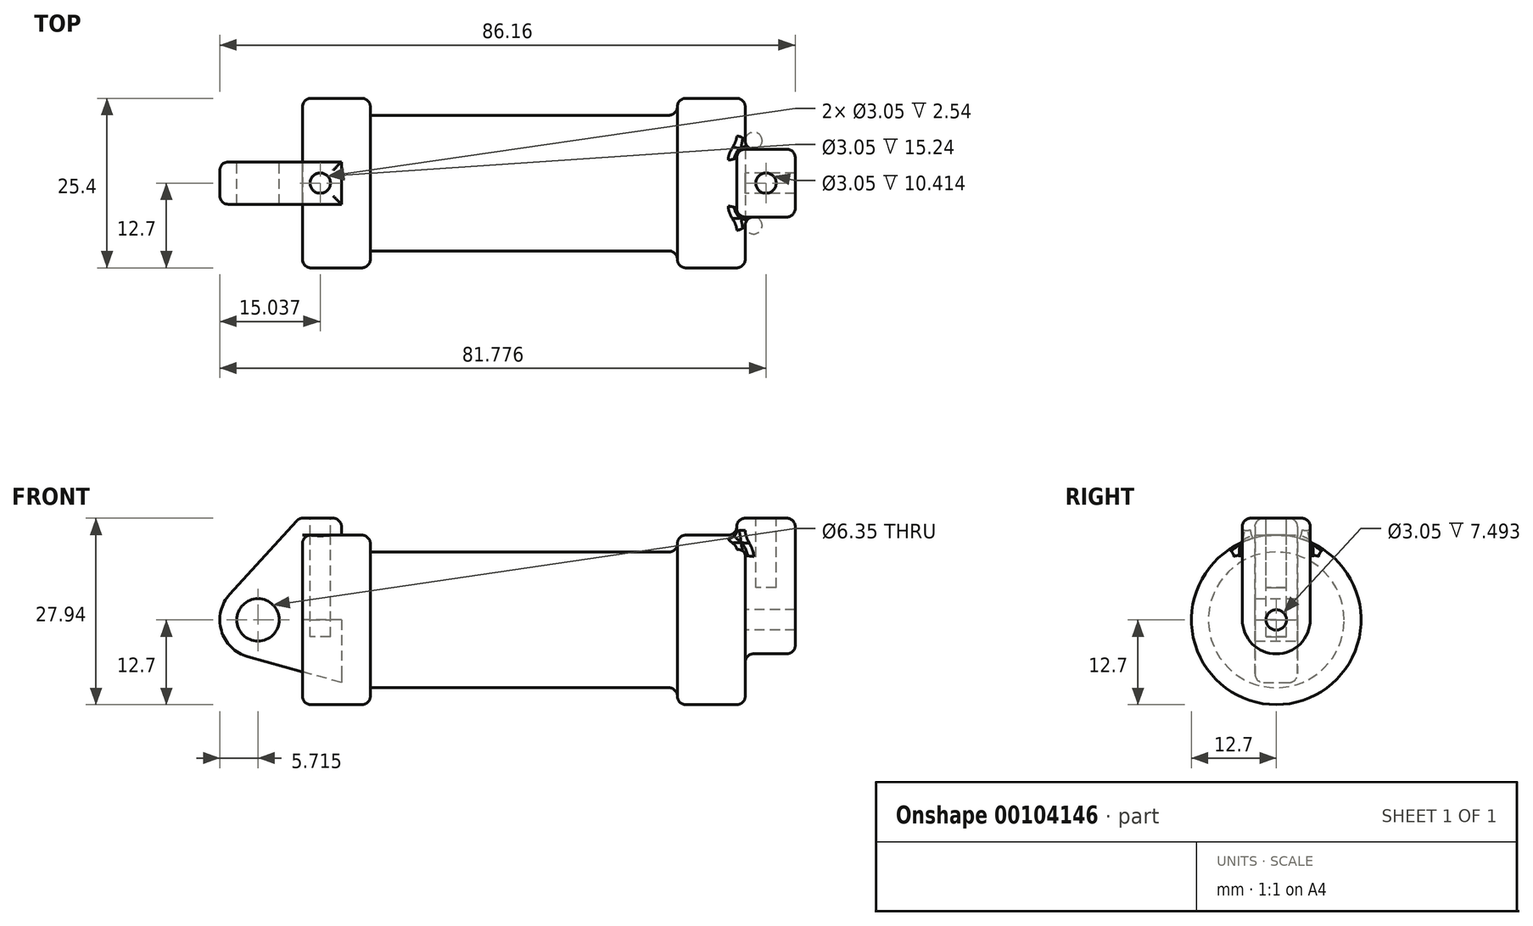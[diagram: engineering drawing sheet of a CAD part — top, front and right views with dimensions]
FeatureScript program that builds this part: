
annotation { "Feature Type Name" : "Feature", "Feature Type Description" : "" }
export const myFeature = defineFeature(function(context is Context, id is Id, definition is map)
    precondition{}
    {
        {
            var Q0;
            Q0=qCreatedBy(makeId("Front.planeOp"),FACE);
            var sketch = newSketch(context, id + "F0", { "sketchPlane" : qUnion([Q0])});
            skLineSegment(sketch, "E0", {"start": v(0, 0) * mm, "end": v(0, 12.7) * mm});
            skLineSegment(sketch, "E1", {"start": v(0, 12.7) * mm, "end": v(10.16, 12.7) * mm});
            skLineSegment(sketch, "E2", {"start": v(10.16, 12.7) * mm, "end": v(10.16, 10.16) * mm});
            skLineSegment(sketch, "E3", {"start": v(10.16, 10.16) * mm, "end": v(56.13, 10.16) * mm});
            skLineSegment(sketch, "E4", {"start": v(56.13, 10.16) * mm, "end": v(56.13, 12.7) * mm});
            skLineSegment(sketch, "E5", {"start": v(56.13, 12.7) * mm, "end": v(66.3, 12.7) * mm});
            skLineSegment(sketch, "E6", {"start": v(66.3, 12.7) * mm, "end": v(66.3, 0) * mm});
            skLineSegment(sketch, "E7", {"start": v(66.3, 0) * mm, "end": v(0, 0) * mm});
            skLineSegment(sketch, "E8", {"start": v(5.84, 15.24) * mm, "end": v(-0.5, 15.24) * mm});
            skLineSegment(sketch, "E9", {"start": v(-0.5, 15.24) * mm, "end": v(-10.88, 3.85) * mm});
            skLineSegment(sketch, "E10", {"start": v(0, 0) * mm, "end": v(-6.65, 0) * mm});
            skCircle(sketch, "E11", {"center": v(-6.65, 0) * mm, "radius": 5.72 * mm});
            skCircle(sketch, "E12", {"center": v(-6.65, 0) * mm, "radius": 3.18 * mm});
            skLineSegment(sketch, "E13", {"start": v(5.84, 15.24) * mm, "end": v(5.84, -9.4) * mm});
            skLineSegment(sketch, "E14", {"start": v(5.84, -9.4) * mm, "end": v(-8.18, -5.5) * mm});
            skSolve(sketch);
        }
        {
            var Q0;
            {var subQ0=sQuery(id+"F0.wireOp",EDGE,"E2");Q0=makeQuery(id+"F0.imprint","IMPRINT",FACE,{"disambiguationData":[TD([[makeQuery(id+"F0.imprint","IMPRINT",EDGE,{"derivedFrom":subQ0}),-1.0]])]});}
            var Q1;
            Q1=sQuery(id+"F0.wireOp",EDGE,"E7");
            revolve(context, id + "F1", {"entities" : qUnion([Q0]), "axis" : qUnion([Q1]), "revolveType" : RevolveType.FULL});
        }
        {
            var Q0;
            {var subQ0=sQuery(id+"F0.wireOp",EDGE,"E0");Q0=makeQuery(id+"F0.imprint","IMPRINT",FACE,{"disambiguationData":[TD([[makeQuery(id+"F0.imprint","IMPRINT",EDGE,{"derivedFrom":subQ0}),-1.0]])]});}
            var Q1;
            Q1=sQuery(id+"F0.wireOp",EDGE,"E7");
            revolve(context, id + "F2", {"operationType" : NewBodyOperationType.ADD, "entities" : qUnion([Q0]), "axis" : qUnion([Q1]), "revolveType" : RevolveType.FULL});
        }
        {
            var Q0;
            {var subQ3=sQuery(id+"F0.wireOp",EDGE,"E0");Q0=makeQuery(id+"F0.imprint","IMPRINT",FACE,{"disambiguationData":[TD([[makeQuery(id+"F0.imprint","IMPRINT",EDGE,{"derivedFrom":subQ3}),1.0]])]});}
            var Q1;
            {var subQ0=sQuery(id+"F0.wireOp",EDGE,"E14");Q1=makeQuery(id+"F0.imprint","IMPRINT",FACE,{"disambiguationData":[TD([[makeQuery(id+"F0.imprint","IMPRINT",EDGE,{"derivedFrom":subQ0}),-1.0]])]});}
            var Q2;
            {var subQ4=sQuery(id+"F0.wireOp",EDGE,"E12");Q2=makeQuery(id+"F0.imprint","IMPRINT",FACE,{"disambiguationData":[TD([[makeQuery(id+"F0.imprint","IMPRINT",EDGE,{"derivedFrom":subQ4}),-1.0]])]});}
            extrude(context, id + "F3", {"entities" : qUnion([Q0, Q1, Q2]), "endBound" : BoundingType.SYMMETRIC, "depth" : 6.35 * mm});
        }
        {
            var Q0;
            Q0=makeQuery(id+"F1.opRevolve","SWEPT_FACE",FACE,{"disambiguationData":[OSD([sQuery(id+"F0.wireOp",EDGE,"E6")])]});
            var sketch = newSketch(context, id + "F4", { "sketchPlane" : qUnion([Q0])});
            skCircle(sketch, "E15", {"center": v(0, 0) * mm, "radius": 1.52 * mm});
            skCircle(sketch, "E16", {"center": v(0, 0) * mm, "radius": 5.08 * mm});
            skLineSegment(sketch, "E17", {"start": v(-5.08, 0) * mm, "end": v(-5.08, 15.24) * mm});
            skLineSegment(sketch, "E18", {"start": v(5.08, 0) * mm, "end": v(5.08, 15.24) * mm});
            skLineSegment(sketch, "E19", {"start": v(-5.08, 15.24) * mm, "end": v(5.08, 15.24) * mm});
            skSolve(sketch);
        }
        {
            var Q0;
            Q0=makeQuery(id+"F4.imprint","IMPRINT",FACE,{"disambiguationData":[TD([[makeQuery(id+"F4.imprint","IMPRINT",EDGE,{"derivedFrom":sQuery(id+"F4.wireOp",EDGE,"E15")}),-1.0]])]});
            var Q1;
            {var subQ0=sQuery(id+"F4.wireOp",EDGE,"E17");var subQ1=sQuery(id+"F4.wireOp",EDGE,"E16");var subQ2=makeQuery(id+"F4.imprint","INTERSECT",VERTEX,{"derivedFrom":[subQ1,subQ0]});Q1=makeQuery(id+"F4.imprint","IMPRINT",FACE,{"disambiguationData":[TD([[makeQuery(id+"F4.imprint","IMPRINT",EDGE,{"disambiguationData":[TD([[subQ2,1.0]])],"derivedFrom":subQ1}),-1.0]])]});}
            var Q2;
            {var subQ0=sQuery(id+"F4.wireOp",EDGE,"E19");Q2=makeQuery(id+"F4.imprint","IMPRINT",FACE,{"disambiguationData":[TD([[makeQuery(id+"F4.imprint","IMPRINT",EDGE,{"derivedFrom":subQ0}),-1.0]])]});}
            extrude(context, id + "F5", {"entities" : qUnion([Q0, Q1, Q2]), "operationType" : NewBodyOperationType.ADD, "depth" : 7.5 * mm, "hasSecondDirection" : true, "secondDirectionOppositeDirection" : true, "secondDirectionDepth" : 1.27 * mm});
        }
        {
            var Q0;
            Q0=makeQuery(id+"F5.opExtrude","SWEPT_FACE",FACE,{"disambiguationData":[OSD([sQuery(id+"F4.wireOp",EDGE,"E19")])]});
            var sketch = newSketch(context, id + "F6", { "sketchPlane" : qUnion([Q0])});
            skCircle(sketch, "E20", {"center": v(69.4, 0) * mm, "radius": 1.52 * mm});
            skPoint(sketch, "E20.centerSnap0", {"position": v(69.4, 5.08) * mm});
            skPoint(sketch, "E20.centerSnap1", {"position": v(65.02, 0) * mm});
            skSolve(sketch);
        }
        {
            var Q0;
            Q0=makeQuery(id+"F3.opExtrude","SWEPT_FACE",FACE,{"disambiguationData":[OSD([sQuery(id+"F0.wireOp",EDGE,"E8")])]});
            var sketch = newSketch(context, id + "F7", { "sketchPlane" : qUnion([Q0])});
            skCircle(sketch, "E21", {"center": v(2.67, 0) * mm, "radius": 1.52 * mm});
            skPoint(sketch, "E21.centerSnap0", {"position": v(-0.5, 0) * mm});
            skPoint(sketch, "E21.centerSnap1", {"position": v(2.67, 3.18) * mm});
            skSolve(sketch);
        }
        {
            var Q0;
            Q0=makeQuery(id+"F7.imprint","IMPRINT",FACE,{"disambiguationData":[TD([[makeQuery(id+"F7.imprint","IMPRINT",EDGE,{"derivedFrom":sQuery(id+"F7.wireOp",EDGE,"E21")}),1.0]])]});
            extrude(context, id + "F8", {"entities" : qUnion([Q0]), "operationType" : NewBodyOperationType.REMOVE, "oppositeDirection" : true, "depth" : 17.78 * mm});
        }
        {
            var Q0;
            Q0=makeQuery(id+"F6.imprint","IMPRINT",FACE,{"disambiguationData":[TD([[makeQuery(id+"F6.imprint","IMPRINT",EDGE,{"derivedFrom":sQuery(id+"F6.wireOp",EDGE,"E20")}),1.0]])]});
            extrude(context, id + "F9", {"entities" : qUnion([Q0]), "operationType" : NewBodyOperationType.REMOVE, "oppositeDirection" : true, "depth" : 10.4 * mm});
        }
        {
            var Q0;
            Q0=makeQuery(id+"F3.opExtrude","CAP_EDGE",EDGE,{"disambiguationData":[OSD([sQuery(id+"F0.wireOp",EDGE,"E9")])],"isStart":true});
            var Q1;
            Q1=makeQuery(id+"F3.opExtrude","CAP_EDGE",EDGE,{"disambiguationData":[OSD([sQuery(id+"F0.wireOp",EDGE,"E11")])],"isStart":true});
            var Q2;
            Q2=makeQuery(id+"F3.opExtrude","CAP_EDGE",EDGE,{"disambiguationData":[OSD([sQuery(id+"F0.wireOp",EDGE,"E14")])],"isStart":true});
            var Q3;
            Q3=makeQuery(id+"F3.opExtrude","CAP_EDGE",EDGE,{"disambiguationData":[OSD([sQuery(id+"F0.wireOp",EDGE,"E14")])],"isStart":false});
            var Q4;
            Q4=makeQuery(id+"F3.opExtrude","CAP_EDGE",EDGE,{"disambiguationData":[OSD([sQuery(id+"F0.wireOp",EDGE,"E11")])],"isStart":false});
            var Q5;
            Q5=makeQuery(id+"F3.opExtrude","CAP_EDGE",EDGE,{"disambiguationData":[OSD([sQuery(id+"F0.wireOp",EDGE,"E9")])],"isStart":false});
            var Q6;
            Q6=makeQuery(id+"F3.opExtrude","SWEPT_EDGE",EDGE,{"disambiguationData":[OSD([sQuery(id+"F0.wireOp",EDGE,"E8"),sQuery(id+"F0.wireOp",EDGE,"E9")])]});
            var Q7;
            Q7=makeQuery(id+"F3.opExtrude","CAP_EDGE",EDGE,{"disambiguationData":[OSD([sQuery(id+"F0.wireOp",EDGE,"E8")])],"isStart":true});
            var Q8;
            Q8=makeQuery(id+"F3.opExtrude","SWEPT_EDGE",EDGE,{"disambiguationData":[OSD([sQuery(id+"F0.wireOp",EDGE,"E8"),sQuery(id+"F0.wireOp",EDGE,"E13")])]});
            var Q9;
            Q9=makeQuery(id+"F3.opExtrude","CAP_EDGE",EDGE,{"disambiguationData":[OSD([sQuery(id+"F0.wireOp",EDGE,"E8")])],"isStart":false});
            var Q10;
            Q10=makeQuery(id+"F2.opRevolve","SWEPT_EDGE",EDGE,{"disambiguationData":[OSD([sQuery(id+"F0.wireOp",EDGE,"E0"),sQuery(id+"F0.wireOp",EDGE,"E1")])]});
            var Q11;
            Q11=makeQuery(id+"F1.opRevolve","SWEPT_EDGE",EDGE,{"disambiguationData":[OSD([sQuery(id+"F0.wireOp",EDGE,"E1"),sQuery(id+"F0.wireOp",EDGE,"E2")])]});
            fillet(context, id + "F10", {"entities" : qUnion([Q0, Q1, Q2, Q3, Q4, Q5, Q6, Q7, Q8, Q9, Q10, Q11]), "radius" : 1.27 * mm, "tangentPropagation" : true, "allowEdgeOverflow" : false});
        }
        {
            var Q0;
            Q0=makeQuery(id+"F1.opRevolve","SWEPT_EDGE",EDGE,{"disambiguationData":[OSD([sQuery(id+"F0.wireOp",EDGE,"E5"),sQuery(id+"F0.wireOp",EDGE,"E6")])]});
            var Q1;
            Q1=makeQuery(id+"F1.opRevolve","SWEPT_EDGE",EDGE,{"disambiguationData":[OSD([sQuery(id+"F0.wireOp",EDGE,"E4"),sQuery(id+"F0.wireOp",EDGE,"E5")])]});
            var Q2;
            Q2=makeQuery(id+"F5.opExtrude","SWEPT_EDGE",EDGE,{"disambiguationData":[OSD([sQuery(id+"F4.wireOp",EDGE,"E18"),sQuery(id+"F4.wireOp",EDGE,"E19")])]});
            var Q3;
            Q3=makeQuery(id+"F5.opExtrude","CAP_EDGE",EDGE,{"disambiguationData":[OSD([sQuery(id+"F4.wireOp",EDGE,"E19")])],"isStart":true});
            var Q4;
            Q4=makeQuery(id+"F5.opExtrude","SWEPT_EDGE",EDGE,{"disambiguationData":[OSD([sQuery(id+"F4.wireOp",EDGE,"E17"),sQuery(id+"F4.wireOp",EDGE,"E19")])]});
            var Q5;
            Q5=makeQuery(id+"F5.opExtrude","CAP_EDGE",EDGE,{"disambiguationData":[OSD([sQuery(id+"F4.wireOp",EDGE,"E19")])],"isStart":false});
            var Q6;
            Q6=makeQuery(id+"F5.opExtrude","CAP_EDGE",EDGE,{"disambiguationData":[OSD([sQuery(id+"F4.wireOp",EDGE,"E18")])],"isStart":false});
            var Q7;
            Q7=makeQuery(id+"F5.boolean.opBoolean","INTERSECT",EDGE,{"derivedFrom":[makeQuery(id+"F1.opRevolve","SWEPT_FACE",FACE,{"disambiguationData":[OSD([sQuery(id+"F0.wireOp",EDGE,"E6")])]}),makeQuery(id+"F5.opExtrude","SWEPT_FACE",FACE,{"disambiguationData":[OSD([sQuery(id+"F4.wireOp",EDGE,"E18")])]})]});
            var Q8;
            Q8=makeQuery(id+"F5.boolean.opBoolean","INTERSECT",EDGE,{"derivedFrom":[makeQuery(id+"F1.opRevolve","SWEPT_FACE",FACE,{"disambiguationData":[OSD([sQuery(id+"F0.wireOp",EDGE,"E5")])]}),makeQuery(id+"F5.opExtrude","SWEPT_FACE",FACE,{"disambiguationData":[OSD([sQuery(id+"F4.wireOp",EDGE,"E18")])]})]});
            var Q9;
            Q9=makeQuery(id+"F5.opExtrude","CAP_EDGE",EDGE,{"disambiguationData":[OSD([sQuery(id+"F4.wireOp",EDGE,"E18")])],"isStart":true});
            var Q10;
            Q10=makeQuery(id+"F5.opExtrude","SWEPT_EDGE",EDGE,{"disambiguationData":[OSD([sQuery(id+"F4.wireOp",EDGE,"E16"),sQuery(id+"F4.wireOp",EDGE,"E18")])]});
            var Q11;
            Q11=makeQuery(id+"F5.opExtrude","SWEPT_EDGE",EDGE,{"disambiguationData":[OSD([sQuery(id+"F4.wireOp",EDGE,"E16"),sQuery(id+"F4.wireOp",EDGE,"E17")])]});
            var Q12;
            Q12=makeQuery(id+"F5.opExtrude","CAP_EDGE",EDGE,{"disambiguationData":[OSD([sQuery(id+"F4.wireOp",EDGE,"E17")])],"isStart":false});
            var Q13;
            Q13=makeQuery(id+"F5.boolean.opBoolean","INTERSECT",EDGE,{"derivedFrom":[makeQuery(id+"F1.opRevolve","SWEPT_FACE",FACE,{"disambiguationData":[OSD([sQuery(id+"F0.wireOp",EDGE,"E6")])]}),makeQuery(id+"F5.opExtrude","SWEPT_FACE",FACE,{"disambiguationData":[OSD([sQuery(id+"F4.wireOp",EDGE,"E17")])]})]});
            var Q14;
            Q14=makeQuery(id+"F5.opExtrude","CAP_EDGE",EDGE,{"disambiguationData":[OSD([sQuery(id+"F4.wireOp",EDGE,"E17")])],"isStart":true});
            var Q15;
            Q15=makeQuery(id+"F5.opExtrude","CAP_EDGE",EDGE,{"disambiguationData":[OSD([sQuery(id+"F4.wireOp",EDGE,"E16")])],"isStart":false});
            var Q16;
            Q16=makeQuery(id+"F5.boolean.opBoolean","INTERSECT",EDGE,{"derivedFrom":[makeQuery(id+"F1.opRevolve","SWEPT_FACE",FACE,{"disambiguationData":[OSD([sQuery(id+"F0.wireOp",EDGE,"E6")])]}),makeQuery(id+"F5.opExtrude","SWEPT_FACE",FACE,{"disambiguationData":[OSD([sQuery(id+"F4.wireOp",EDGE,"E16")])]})]});
            var Q17;
            Q17=makeQuery(id+"F5.boolean.opBoolean","INTERSECT",EDGE,{"derivedFrom":[makeQuery(id+"F1.opRevolve","SWEPT_FACE",FACE,{"disambiguationData":[OSD([sQuery(id+"F0.wireOp",EDGE,"E5")])]}),makeQuery(id+"F5.opExtrude","SWEPT_FACE",FACE,{"disambiguationData":[OSD([sQuery(id+"F4.wireOp",EDGE,"E17")])]})]});
            var Q18;
            Q18=makeQuery(id+"F5.boolean.opBoolean","INTERSECT",EDGE,{"derivedFrom":[makeQuery(id+"F1.opRevolve","SWEPT_FACE",FACE,{"disambiguationData":[OSD([sQuery(id+"F0.wireOp",EDGE,"E5")])]}),makeQuery(id+"F5.opExtrude","CAP_FACE",FACE,{"disambiguationData":[OSD([sQuery(id+"F4.wireOp",EDGE,"E15"),sQuery(id+"F4.wireOp",EDGE,"E16"),sQuery(id+"F4.wireOp",EDGE,"E17"),sQuery(id+"F4.wireOp",EDGE,"E18"),sQuery(id+"F4.wireOp",EDGE,"E19")])],"isStart":true})]});
            var Q19;
            Q19=makeQuery(id+"F1.opRevolve","SWEPT_EDGE",EDGE,{"disambiguationData":[OSD([sQuery(id+"F0.wireOp",EDGE,"E3"),sQuery(id+"F0.wireOp",EDGE,"E4")])]});
            fillet(context, id + "F11", {"entities" : qUnion([Q0, Q1, Q2, Q3, Q4, Q5, Q6, Q7, Q8, Q9, Q10, Q11, Q12, Q13, Q14, Q15, Q16, Q17, Q18, Q19]), "radius" : 1.27 * mm, "tangentPropagation" : true, "allowEdgeOverflow" : false});
        }
    });
